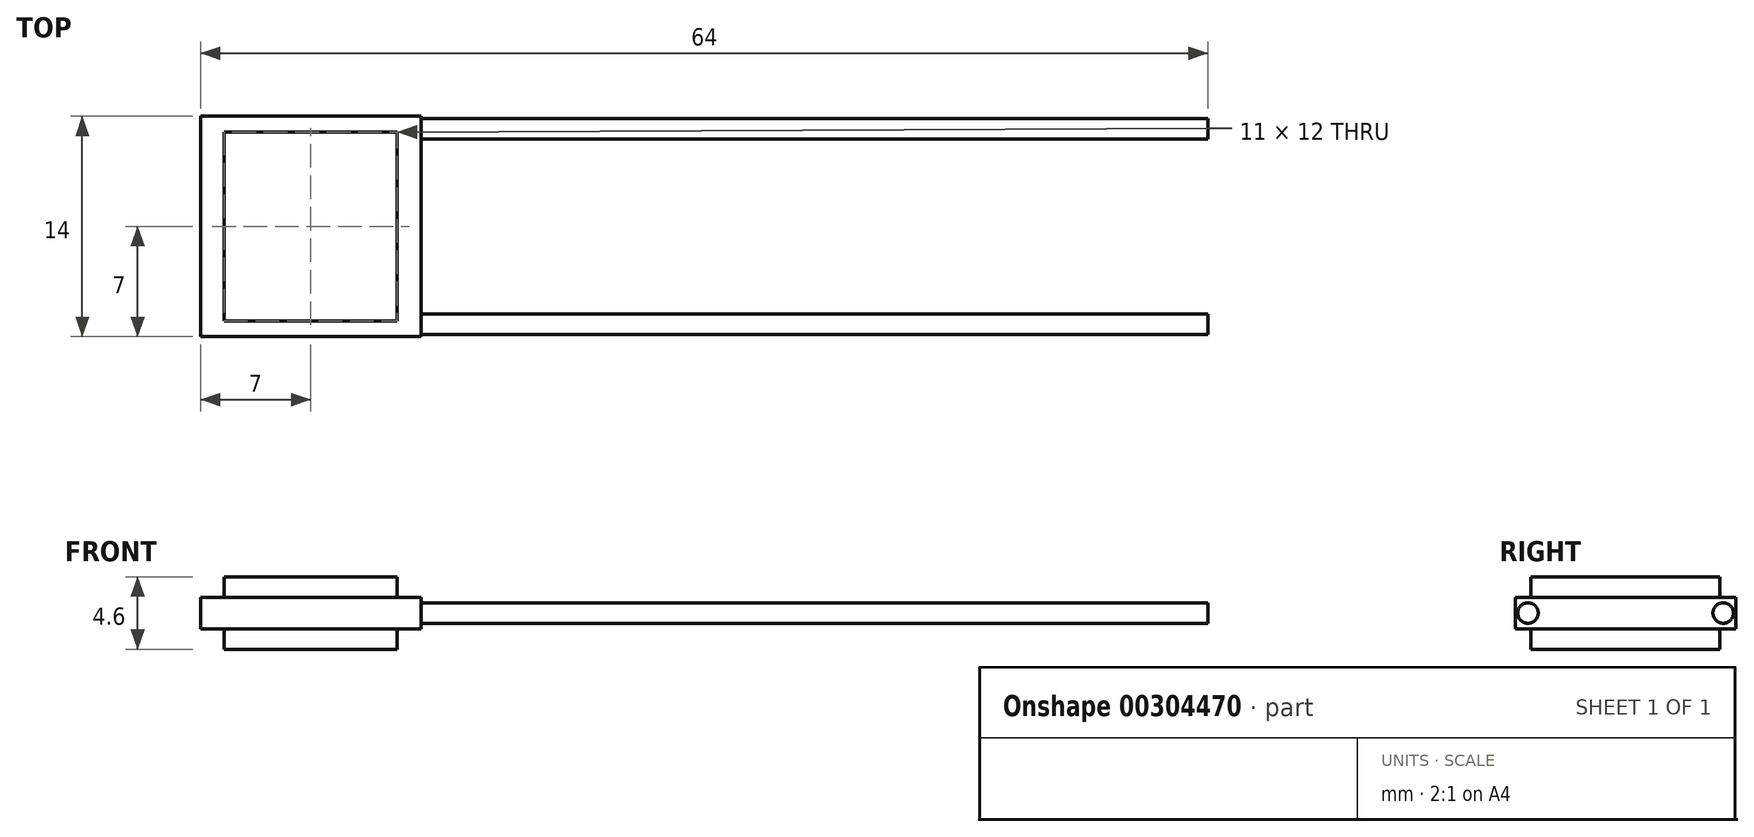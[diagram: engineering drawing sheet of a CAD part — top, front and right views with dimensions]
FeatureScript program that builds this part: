
annotation { "Feature Type Name" : "Feature", "Feature Type Description" : "" }
export const myFeature = defineFeature(function(context is Context, id is Id, definition is map)
    precondition{}
    {
        {
            var Q0;
            Q0=qCreatedBy(makeId("Top.planeOp"),FACE);
            var sketch = newSketch(context, id + "F0", { "sketchPlane" : qUnion([Q0])});
            skLineSegment(sketch, "E0.bottom", {"start": v(5.5, -6) * mm, "end": v(-5.5, -6) * mm});
            skLineSegment(sketch, "E0.top", {"start": v(5.5, 6) * mm, "end": v(-5.5, 6) * mm});
            skLineSegment(sketch, "E0.left", {"start": v(5.5, -6) * mm, "end": v(5.5, 6) * mm});
            skLineSegment(sketch, "E0.right", {"start": v(-5.5, -6) * mm, "end": v(-5.5, 6) * mm});
            skPoint(sketch, "E0.middle", {"position": v(0, 0) * mm});
            skSolve(sketch);
        }
        {
            var Q0;
            Q0 = qSketchRegion(id + "F0", true);
            extrude(context, id + "F1", {"entities" : qUnion([Q0]), "oppositeDirection" : true, "depth" : 1.3 * mm});
        }
        {
            var Q0;
            Q0=makeQuery(id+"F1.opExtrude","CAP_FACE",FACE,{"disambiguationData":[OSD([sQuery(id+"F0.wireOp",EDGE,"E0.bottom"),sQuery(id+"F0.wireOp",EDGE,"E0.top"),sQuery(id+"F0.wireOp",EDGE,"E0.left"),sQuery(id+"F0.wireOp",EDGE,"E0.right")])],"isStart":true});
            var sketch = newSketch(context, id + "F2", { "sketchPlane" : qUnion([Q0])});
            skLineSegment(sketch, "E1.bottom", {"start": v(7, 7) * mm, "end": v(-7, 7) * mm});
            skLineSegment(sketch, "E1.top", {"start": v(7, -7) * mm, "end": v(-7, -7) * mm});
            skLineSegment(sketch, "E1.left", {"start": v(7, 7) * mm, "end": v(7, -7) * mm});
            skLineSegment(sketch, "E1.right", {"start": v(-7, 7) * mm, "end": v(-7, -7) * mm});
            skPoint(sketch, "E1.middle", {"position": v(0, 0) * mm});
            skSolve(sketch);
        }
        {
            var Q0;
            Q0 = qSketchRegion(id + "F2", true);
            extrude(context, id + "F3", {"entities" : qUnion([Q0]), "operationType" : NewBodyOperationType.ADD, "depth" : 2 * mm});
        }
        {
            var Q0;
            Q0=makeQuery(id+"F3.opExtrude","CAP_FACE",FACE,{"disambiguationData":[OSD([sQuery(id+"F2.wireOp",EDGE,"E1.bottom"),sQuery(id+"F2.wireOp",EDGE,"E1.top"),sQuery(id+"F2.wireOp",EDGE,"E1.left"),sQuery(id+"F2.wireOp",EDGE,"E1.right")])],"isStart":false});
            var sketch = newSketch(context, id + "F4", { "sketchPlane" : qUnion([Q0])});
            skLineSegment(sketch, "E2.bottom", {"start": v(5.5, -6) * mm, "end": v(-5.5, -6) * mm});
            skLineSegment(sketch, "E2.top", {"start": v(5.5, 6) * mm, "end": v(-5.5, 6) * mm});
            skLineSegment(sketch, "E2.left", {"start": v(5.5, -6) * mm, "end": v(5.5, 6) * mm});
            skLineSegment(sketch, "E2.right", {"start": v(-5.5, -6) * mm, "end": v(-5.5, 6) * mm});
            skPoint(sketch, "E2.middle", {"position": v(0, 0) * mm});
            skSolve(sketch);
        }
        {
            var Q0;
            Q0 = qSketchRegion(id + "F4", true);
            extrude(context, id + "F5", {"entities" : qUnion([Q0]), "operationType" : NewBodyOperationType.ADD, "depth" : 1.3 * mm});
        }
        {
            var Q0;
            Q0=makeQuery(id+"F3.opExtrude","SWEPT_FACE",FACE,{"disambiguationData":[OSD([sQuery(id+"F2.wireOp",EDGE,"E1.left")])]});
            var sketch = newSketch(context, id + "F6", { "sketchPlane" : qUnion([Q0])});
            skCircle(sketch, "E3", {"center": v(-6.2, 1) * mm, "radius": 0.65 * mm});
            skPoint(sketch, "E3.centerSnap0", {"position": v(-7, 1) * mm});
            skCircle(sketch, "E4", {"center": v(6.2, 1) * mm, "radius": 0.65 * mm});
            skSolve(sketch);
        }
        {
            var Q0;
            Q0 = qSketchRegion(id + "F6", true);
            extrude(context, id + "F7", {"entities" : qUnion([Q0]), "depth" : 50 * mm});
        }
    });
